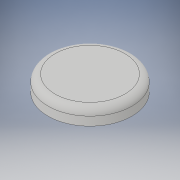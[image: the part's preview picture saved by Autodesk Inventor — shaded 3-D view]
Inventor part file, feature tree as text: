
AUTODESK INVENTOR PART (.ipt)
format: ipt  version: 2017 (Build 210142000, 142)  size: 125,952 bytes
history: native  units: in
note: dims shown in document units (in); Inventor stores cm internally (conversion verified against a paired STEP export)
features: revolve x1, chamfer x1, sketch x1
ambient origin geometry x8: Origin, YZ Plane, XZ Plane, XY Plane, X Axis, Y Axis, Z Axis, Center Point
bodies: Solid1 (feature_tree)
feature tree (3):
  revolve  "Revolution1"  [1 undecoded]
  chamfer  "Chamfer1"  Distance=0.75in
  sketch  "Sketch1"  dims[d0=0.49in d1=0.22in d2=0.75in d3=0.5in d4=0.125in d5=90.0deg d6=0.0625in d7=0.125in d8=45.0deg]
note: 1 required parameter value undecoded (feature->parameter linkage not recoverable at this tier; creation-order binding heuristic only, values carry confidence <= 0.55)
